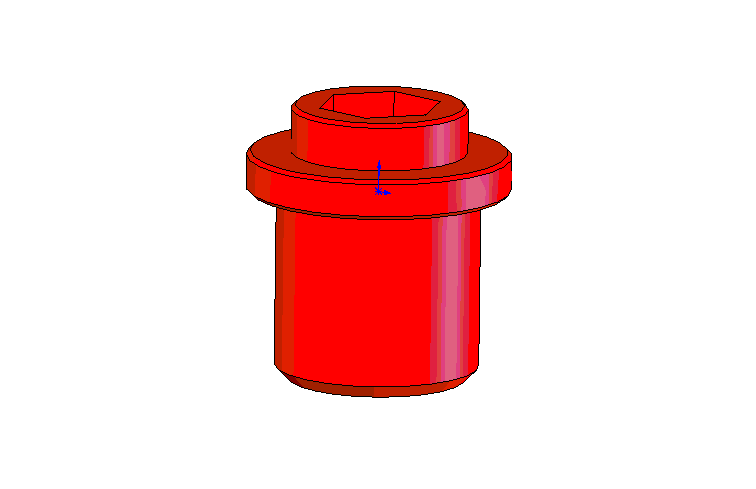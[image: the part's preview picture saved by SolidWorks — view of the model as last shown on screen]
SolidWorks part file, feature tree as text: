
SOLIDWORKS PART (.sldprt)
format: sldprt  version: not decoded by parser v0  size: 201,216 bytes
history: native  units: mm
features: sketch x5, plane x3, extrude x3, cut_extrude x2, chamfer x2, material x1 (+10 scaffold rows collapsed)
feature tree (26):
  scaffold x10  (default folders/planes/origin — collapsed)
  material  "Matériau <non spécifié>"
  plane  "Plan de face"
  plane  "Plan de dessus"
  plane  "Plan de droite"
  sketch  "Esquisse1"  dims[D1=15.0mm]
  extrude  "Extrusion1"  Depth=14mm
  sketch  "Esquisse2"  dims[D1=19.5mm]
  extrude  "Extrusion2"  Depth=3mm
  sketch  "Esquisse3"  dims[D1=13.0mm]
  extrude  "Extrusion3"  Depth=6.5mm
  sketch  "Esquisse4"  dims[D1=9.0mm]
  cut_extrude  "Enlèv. mat.-Extru.1"  Depth=12.5mm
  sketch  "Esquisse5"  dims[D1=8.0mm]
  cut_extrude  "Enlèv. mat.-Extru.2"  Depth=5mm
  chamfer  "Chanfrein1"  Distance=1mm Angle=45deg
  chamfer  "Chanfrein2"  Distance=0.3mm Angle=45deg
decode coverage: 12 of 12 modeling features carry decoded parameters
note: suppression state not decoded; provenance and decode notes live in map.json
